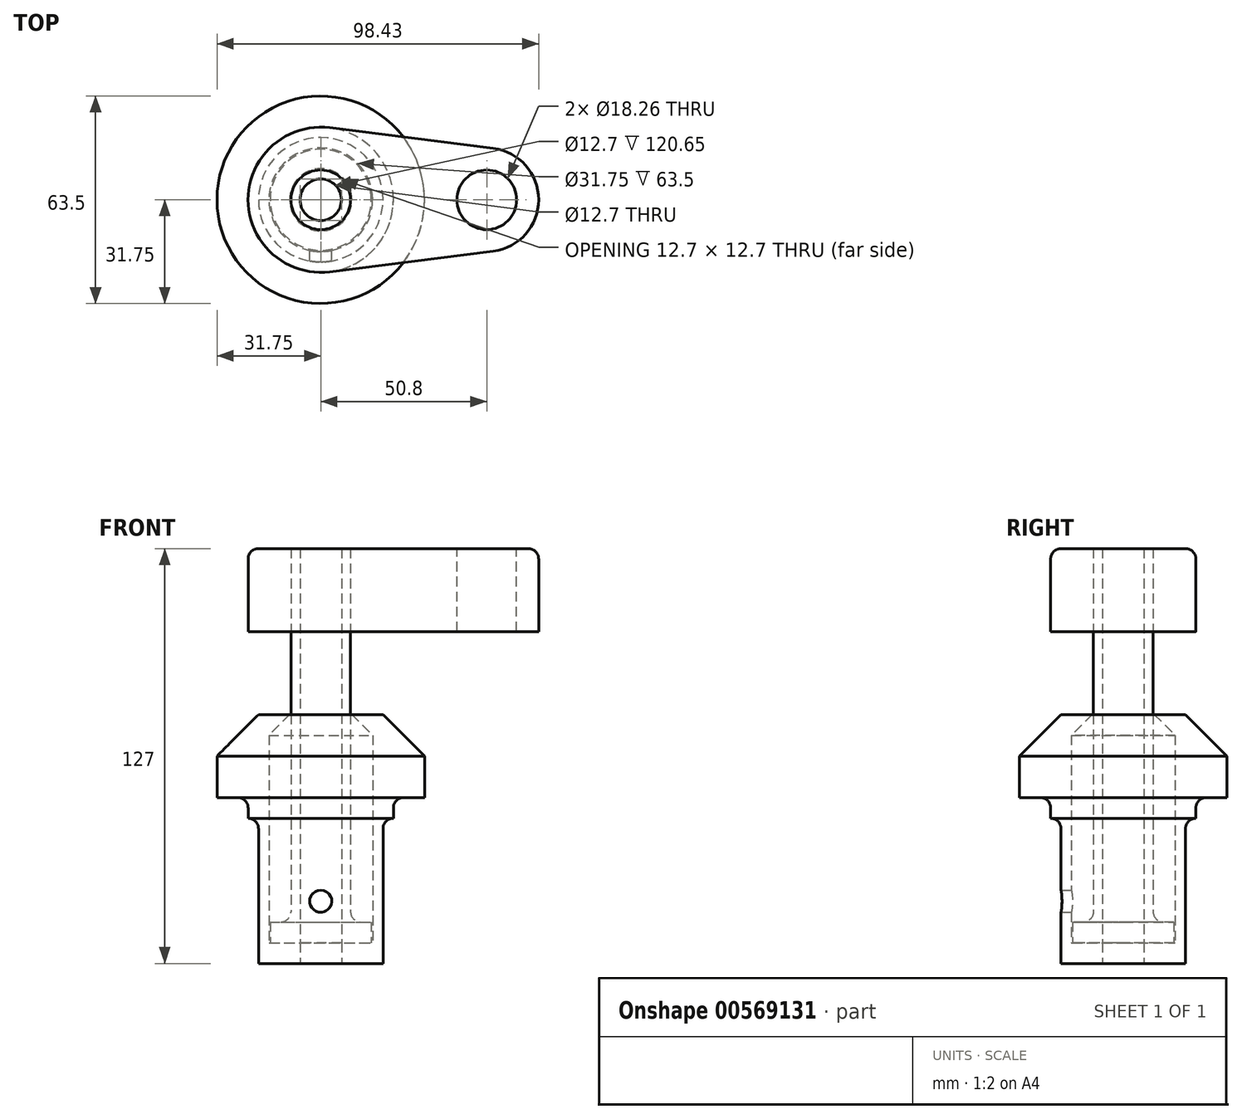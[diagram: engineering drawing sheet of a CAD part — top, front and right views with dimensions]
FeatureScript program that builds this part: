
annotation { "Feature Type Name" : "Feature", "Feature Type Description" : "" }
export const myFeature = defineFeature(function(context is Context, id is Id, definition is map)
    precondition{}
    {
        {
            var Q0;
            Q0=qCreatedBy(makeId("Front.planeOp"),FACE);
            var sketch = newSketch(context, id + "F0", { "sketchPlane" : qUnion([Q0])});
            skLineSegment(sketch, "E0", {"start": v(0, 0) * mm, "end": v(0, 76.2) * mm});
            skLineSegment(sketch, "E1", {"start": v(0, 76.2) * mm, "end": v(19.05, 76.2) * mm});
            skLineSegment(sketch, "E2", {"start": v(19.05, 76.2) * mm, "end": v(31.75, 63.5) * mm});
            skLineSegment(sketch, "E3", {"start": v(31.75, 63.5) * mm, "end": v(31.75, 50.8) * mm});
            skLineSegment(sketch, "E4", {"start": v(31.75, 50.8) * mm, "end": v(22.23, 50.8) * mm});
            skLineSegment(sketch, "E5", {"start": v(22.23, 50.8) * mm, "end": v(22.23, 44.45) * mm});
            skLineSegment(sketch, "E6", {"start": v(22.23, 44.45) * mm, "end": v(19.05, 44.45) * mm});
            skLineSegment(sketch, "E7", {"start": v(19.05, 44.45) * mm, "end": v(19.05, 0) * mm});
            skLineSegment(sketch, "E8", {"start": v(19.05, 0) * mm, "end": v(0, 0) * mm});
            skLineSegment(sketch, "E9", {"start": v(9.52, 76.2) * mm, "end": v(15.88, 69.85) * mm});
            skLineSegment(sketch, "E10", {"start": v(15.88, 69.85) * mm, "end": v(15.88, 6.35) * mm});
            skLineSegment(sketch, "E11", {"start": v(15.88, 6.35) * mm, "end": v(0, 6.35) * mm});
            skLineSegment(sketch, "E12", {"start": v(0, 76.2) * mm, "end": v(0, 92.06) * mm, "construction": true});
            skLineSegment(sketch, "E13", {"start": v(0, 76.2) * mm, "end": v(0, 127) * mm});
            skLineSegment(sketch, "E14", {"start": v(0, 127) * mm, "end": v(9.13, 127) * mm});
            skLineSegment(sketch, "E15", {"start": v(9.13, 127) * mm, "end": v(9.13, 12.7) * mm});
            skLineSegment(sketch, "E16", {"start": v(9.13, 12.7) * mm, "end": v(15.48, 12.7) * mm});
            skLineSegment(sketch, "E17", {"start": v(15.48, 12.7) * mm, "end": v(15.48, 6.35) * mm});
            skSolve(sketch);
        }
        {
            var Q0;
            {var subQ4=sQuery(id+"F0.wireOp",EDGE,"E2");Q0=makeQuery(id+"F0.imprint","IMPRINT",FACE,{"disambiguationData":[TD([[makeQuery(id+"F0.imprint","IMPRINT",EDGE,{"derivedFrom":subQ4}),-1.0]])]});}
            var Q1;
            Q1=sQuery(id+"F0.wireOp",EDGE,"E0");
            revolve(context, id + "F1", {"entities" : qUnion([Q0]), "axis" : qUnion([Q1]), "revolveType" : RevolveType.FULL});
        }
        {
            var Q0;
            {var subQ0=sQuery(id+"F0.wireOp",EDGE,"E13");Q0=makeQuery(id+"F0.imprint","IMPRINT",FACE,{"disambiguationData":[TD([[makeQuery(id+"F0.imprint","IMPRINT",EDGE,{"derivedFrom":subQ0}),-1.0]])]});}
            var Q1;
            {var subQ0=sQuery(id+"F0.wireOp",EDGE,"E16");Q1=makeQuery(id+"F0.imprint","IMPRINT",FACE,{"disambiguationData":[TD([[makeQuery(id+"F0.imprint","IMPRINT",EDGE,{"derivedFrom":subQ0}),-1.0]])]});}
            var Q2;
            Q2=sQuery(id+"F0.wireOp",EDGE,"E13");
            revolve(context, id + "F2", {"entities" : qUnion([Q0, Q1]), "axis" : qUnion([Q2]), "revolveType" : RevolveType.FULL});
        }
        {
            var Q0;
            Q0=makeQuery(id+"F2.opRevolve","SWEPT_FACE",FACE,{"disambiguationData":[OSD([sQuery(id+"F0.wireOp",EDGE,"E14")])]});
            var sketch = newSketch(context, id + "F3", { "sketchPlane" : qUnion([Q0])});
            skCircle(sketch, "E18", {"center": v(0, 0) * mm, "radius": 22.23 * mm});
            skCircle(sketch, "E19", {"center": v(50.8, 0) * mm, "radius": 15.88 * mm});
            skLineSegment(sketch, "E20", {"start": v(2.78, 22.05) * mm, "end": v(52.78, 15.75) * mm});
            skLineSegment(sketch, "E21", {"start": v(2.78, -22.05) * mm, "end": v(52.78, -15.75) * mm});
            skCircle(sketch, "E22.0", {"center": v(0, 0) * mm, "radius": 9.13 * mm});
            skCircle(sketch, "E23", {"center": v(50.8, 0) * mm, "radius": 9.13 * mm});
            skSolve(sketch);
        }
        {
            var Q0;
            Q0 = qSketchRegion(id + "F3", true);
            var Q1;
            Q1=makeQuery(id+"F1.opRevolve","SWEPT_FACE",FACE,{"disambiguationData":[OSD([sQuery(id+"F0.wireOp",EDGE,"E1")])]});
            extrude(context, id + "F4", {"entities" : qUnion([Q0]), "oppositeDirection" : true, "depth" : 25.4 * mm, "endBoundEntityFace" : qUnion([Q1]), "offsetDistance" : 1 / 406.4 * mm});
        }
        {
            var Q0;
            Q0=qCreatedBy(makeId("Front.planeOp"),FACE);
            var sketch = newSketch(context, id + "F5", { "sketchPlane" : qUnion([Q0])});
            skPoint(sketch, "E24", {"position": v(0, 19.05) * mm});
            skSolve(sketch);
        }
        {
            var Q0;
            Q0=sQuery(id+"F5.wireOp",VERTEX,"E24");
            var Q1;
            Q1=makeQuery(id+"F1.opRevolve","SWEPT_BODY",BODY,{"disambiguationData":[OSD([sQuery(id+"F0.wireOp",EDGE,"E0"),sQuery(id+"F0.wireOp",EDGE,"E1"),sQuery(id+"F0.wireOp",EDGE,"E2"),sQuery(id+"F0.wireOp",EDGE,"E3"),sQuery(id+"F0.wireOp",EDGE,"E4"),sQuery(id+"F0.wireOp",EDGE,"E5"),sQuery(id+"F0.wireOp",EDGE,"E6"),sQuery(id+"F0.wireOp",EDGE,"E7"),sQuery(id+"F0.wireOp",EDGE,"E8"),sQuery(id+"F0.wireOp",EDGE,"E9"),sQuery(id+"F0.wireOp",EDGE,"E10"),sQuery(id+"F0.wireOp",EDGE,"E11")])]});
            hole(context, id + "F6", {"style" : HoleStyle.SIMPLE, "endStyle" : HoleEndStyle.THROUGH, "oppositeDirection" : true, "standardTappedOrClearance" : lookupTablePath({ "standard" : "ANSI", "fit" : "Normal (ASME)", "size" : "1/4", "type" : "Clearance" }), "standardBlindInLast" : lookupTablePath({ "fit" : "Free", "standard" : "ANSI", "size" : "1/4", "type" : "Clearance" }), "holeDiameter" : 6.76 * mm, "tappedDepth" : 14.3 * mm, "tapClearance" : 3, "locations" : qUnion([Q0]), "scope" : qUnion([Q1])});
        }
        {
            var Q0;
            Q0=makeQuery(id+"F4.opExtrude","CAP_EDGE",EDGE,{"disambiguationData":[OSD([sQuery(id+"F3.wireOp",EDGE,"E18")])],"isStart":true});
            var Q1;
            Q1=makeQuery(id+"F1.opRevolve","SWEPT_EDGE",EDGE,{"disambiguationData":[OSD([sQuery(id+"F0.wireOp",EDGE,"E4"),sQuery(id+"F0.wireOp",EDGE,"E5")])]});
            var Q2;
            Q2=makeQuery(id+"F1.opRevolve","SWEPT_EDGE",EDGE,{"disambiguationData":[OSD([sQuery(id+"F0.wireOp",EDGE,"E6"),sQuery(id+"F0.wireOp",EDGE,"E7")])]});
            var Q3;
            Q3=makeQuery(id+"F2.opRevolve","SWEPT_EDGE",EDGE,{"disambiguationData":[OSD([sQuery(id+"F0.wireOp",EDGE,"E15"),sQuery(id+"F0.wireOp",EDGE,"E16")])]});
            fillet(context, id + "F7", {"entities" : qUnion([Q0, Q1, Q2, Q3]), "radius" : 3.17 * mm, "tangentPropagation" : true, "allowEdgeOverflow" : false});
        }
        {
            var Q0;
            Q0=makeQuery(id+"F1.opRevolve","SWEPT_FACE",FACE,{"disambiguationData":[OSD([sQuery(id+"F0.wireOp",EDGE,"E8")])]});
            var sketch = newSketch(context, id + "F8", { "sketchPlane" : qUnion([Q0])});
            skCircle(sketch, "E25", {"center": v(0, 0) * mm, "radius": 6.35 * mm});
            skSolve(sketch);
        }
        {
            var Q0;
            Q0 = qSketchRegion(id + "F8", true);
            extrude(context, id + "F9", {"entities" : qUnion([Q0]), "operationType" : NewBodyOperationType.REMOVE, "endBound" : BoundingType.THROUGH_ALL, "oppositeDirection" : true, "depth" : 25.4 * mm, "offsetDistance" : 25.4 * mm});
        }
    });
